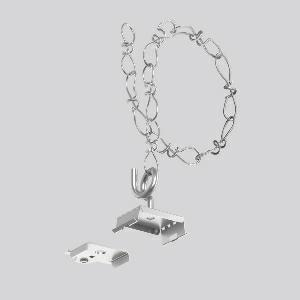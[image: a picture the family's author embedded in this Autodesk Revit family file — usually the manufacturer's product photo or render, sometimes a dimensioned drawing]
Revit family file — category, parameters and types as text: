
# Revit family: linedo_pendelset_1_5m_kette_982662_000_5b74
name_source: partatom
category: Lighting Fixtures
units: mm (PartAtom-declared; Revit-internal decimal feet)

## family parameters
Cut with Voids When Loaded = No
Host = Face
Light Source = No
Part Type = Normal
Room Calculation Point = No
Round Connector Dimension = Use Diameter
Shared = No

## types (1)
- LINEDO Pendelset 1,5m Kette
    Apparent Load = 0 VA
    Default Elevation = 1800 mm
    Description = Suspension kit with chain 1,500 mm. Spring steel, blank, for installing continuous line luminaire modules.
Colour: stainless steel
Weight: 240 g
Type of Installation: pendant
    Height = 40 mm  [stored 0.131234 ft]
    Lamp = 0 x
    Length = 52 mm  [stored 0.170604 ft]
    Luminous efficacy = 0 lm/W
    Manufacturer = RZB
    ModVariant = No
    Model = 982662.000
    Mounting Place = Ceiling
    Mounting Type = Surface mounted
    Number of Poles = 1
    OnlyDefault = Yes
    Power Factor = 1
    Product Name = LINEDO Pendelset 1,5m Kette
    Product group = Surface mounted continuous line luminaire system
    ProductGroupID = 310
    Protection Class = Protection class
    Protection Degree = Degree of protection
    RLX_Detail_Level = 1
    RLX_Emergency_Light_Flux = 0 lm
    RLX_Emergency_Type = 0
    RLX_Emergency_Type_DB = No
    RlxData = <blob elided: 23241 chars, md5=b7d87b9a>
    Standby Power = 0 W
    System Light Flux = 0 lm
    System Power = 0 W
    Type Comments = Product without accessories
    Type Image = 982662.000.jpg
    URL = http://relux.com
    VarID = ---
    Voltage = 0 V
    Weight = 0.00 kg
    Width = 54 mm

note: [stored X ft] marks values corroborated as IEEE doubles in the binary element streams (Revit-internal decimal feet)

## geometry (parser evidence)
native form markers: Blend x4, Sweep x11
no freeform markers — native parametric forms only
